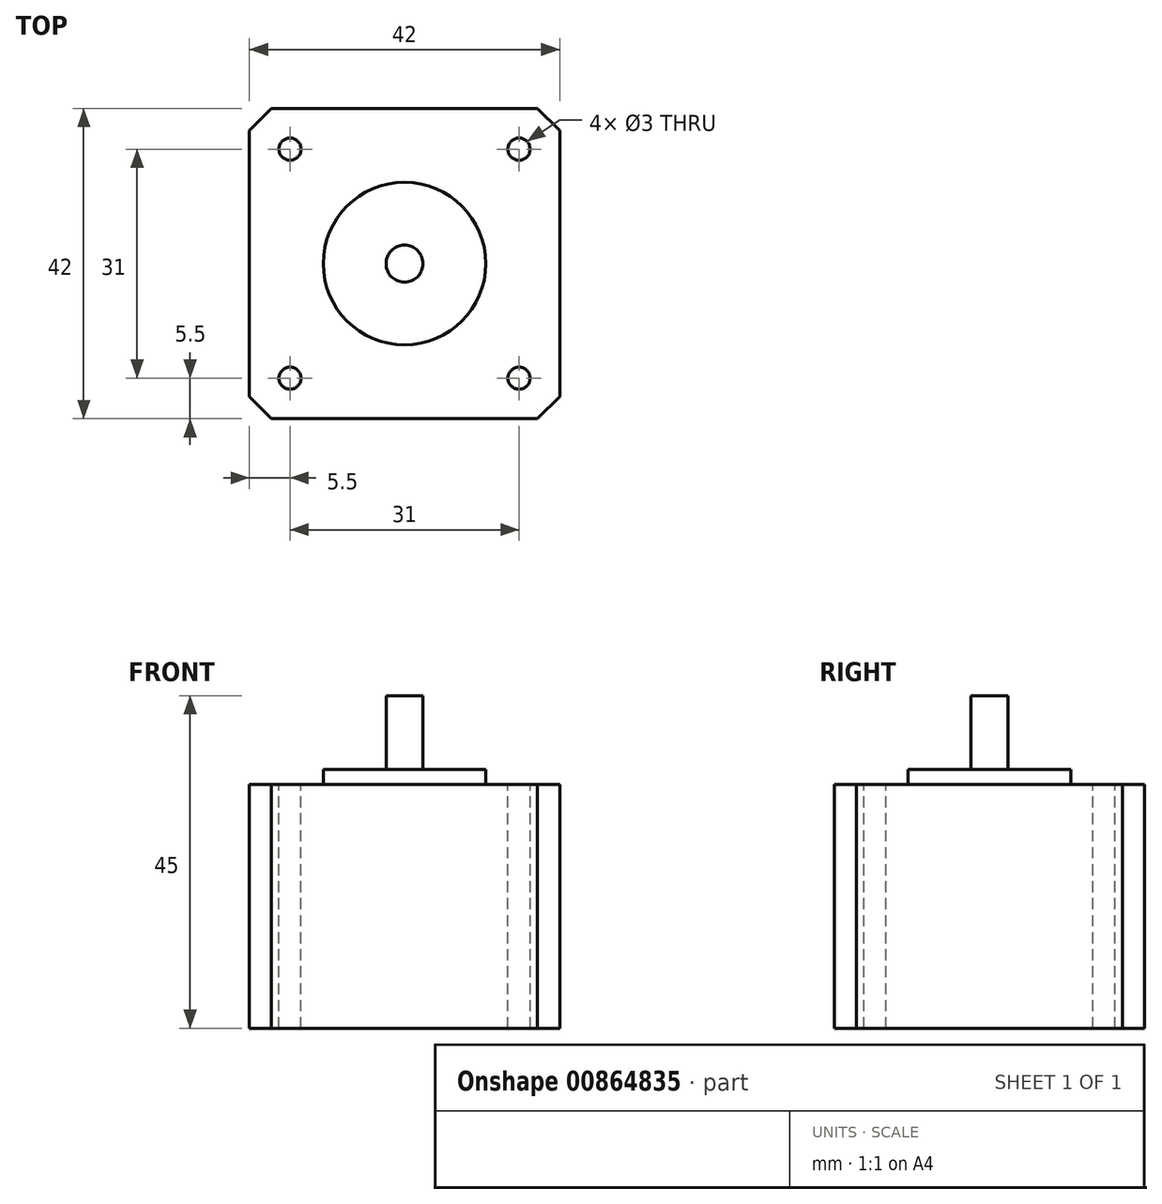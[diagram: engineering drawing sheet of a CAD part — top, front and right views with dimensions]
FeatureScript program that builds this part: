
annotation { "Feature Type Name" : "Feature", "Feature Type Description" : "" }
export const myFeature = defineFeature(function(context is Context, id is Id, definition is map)
    precondition{}
    {
        {
            var Q0;
            Q0=qCreatedBy(makeId("Top.planeOp"),FACE);
            var sketch = newSketch(context, id + "F0", { "sketchPlane" : qUnion([Q0])});
            skLineSegment(sketch, "E0.bottom", {"start": v(21, -21) * mm, "end": v(-21, -21) * mm});
            skLineSegment(sketch, "E0.top", {"start": v(21, 21) * mm, "end": v(-21, 21) * mm});
            skLineSegment(sketch, "E0.left", {"start": v(21, -21) * mm, "end": v(21, 21) * mm});
            skLineSegment(sketch, "E0.right", {"start": v(-21, -21) * mm, "end": v(-21, 21) * mm});
            skPoint(sketch, "E0.middle", {"position": v(0, 0) * mm});
            skSolve(sketch);
        }
        {
            var Q0;
            Q0 = qSketchRegion(id + "F0", true);
            extrude(context, id + "F1", {"entities" : qUnion([Q0]), "depth" : 33 * mm, "offsetDistance" : 25 * mm});
        }
        {
            var Q0;
            Q0=makeQuery(id+"F1.opExtrude","CAP_FACE",FACE,{"disambiguationData":[OSD([sQuery(id+"F0.wireOp",EDGE,"E0.bottom"),sQuery(id+"F0.wireOp",EDGE,"E0.top"),sQuery(id+"F0.wireOp",EDGE,"E0.left"),sQuery(id+"F0.wireOp",EDGE,"E0.right")])],"isStart":false});
            var sketch = newSketch(context, id + "F2", { "sketchPlane" : qUnion([Q0])});
            skCircle(sketch, "E1", {"center": v(0, 0) * mm, "radius": 11 * mm});
            skSolve(sketch);
        }
        {
            var Q0;
            Q0=makeQuery(id+"F2.imprint","IMPRINT",FACE,{"disambiguationData":[TD([[makeQuery(id+"F2.imprint","IMPRINT",EDGE,{"derivedFrom":sQuery(id+"F2.wireOp",EDGE,"E1")}),1.0]])]});
            extrude(context, id + "F3", {"entities" : qUnion([Q0]), "operationType" : NewBodyOperationType.ADD, "depth" : 2 * mm, "offsetDistance" : 25 * mm});
        }
        {
            var Q0;
            Q0=makeQuery(id+"F3.opExtrude","CAP_FACE",FACE,{"disambiguationData":[OSD([sQuery(id+"F2.wireOp",EDGE,"E1")])],"isStart":false});
            var sketch = newSketch(context, id + "F4", { "sketchPlane" : qUnion([Q0])});
            skCircle(sketch, "E2", {"center": v(0, 0) * mm, "radius": 2.5 * mm});
            skSolve(sketch);
        }
        {
            var Q0;
            Q0=makeQuery(id+"F4.imprint","IMPRINT",FACE,{"disambiguationData":[TD([[makeQuery(id+"F4.imprint","IMPRINT",EDGE,{"derivedFrom":sQuery(id+"F4.wireOp",EDGE,"E2")}),1.0]])]});
            extrude(context, id + "F5", {"entities" : qUnion([Q0]), "operationType" : NewBodyOperationType.ADD, "depth" : 10 * mm, "offsetDistance" : 25 * mm});
        }
        {
            var Q0;
            Q0=makeQuery(id+"F1.opExtrude","CAP_FACE",FACE,{"disambiguationData":[OSD([sQuery(id+"F0.wireOp",EDGE,"E0.bottom"),sQuery(id+"F0.wireOp",EDGE,"E0.top"),sQuery(id+"F0.wireOp",EDGE,"E0.left"),sQuery(id+"F0.wireOp",EDGE,"E0.right")])],"isStart":false});
            var sketch = newSketch(context, id + "F6", { "sketchPlane" : qUnion([Q0])});
            skCircle(sketch, "E3", {"center": v(-15.5, 15.5) * mm, "radius": 1.5 * mm});
            skCircle(sketch, "E4", {"center": v(15.5, 15.5) * mm, "radius": 1.5 * mm});
            skCircle(sketch, "E5", {"center": v(15.5, -15.5) * mm, "radius": 1.5 * mm});
            skCircle(sketch, "E6", {"center": v(-15.5, -15.5) * mm, "radius": 1.5 * mm});
            skSolve(sketch);
        }
        {
            var Q0;
            Q0 = qSketchRegion(id + "F6", true);
            extrude(context, id + "F7", {"entities" : qUnion([Q0]), "operationType" : NewBodyOperationType.REMOVE, "endBound" : BoundingType.THROUGH_ALL, "oppositeDirection" : true, "depth" : 25 * mm, "offsetDistance" : 25 * mm});
        }
        {
            var Q0;
            Q0=makeQuery(id+"F1.opExtrude","SWEPT_EDGE",EDGE,{"disambiguationData":[OSD([sQuery(id+"F0.wireOp",EDGE,"E0.top"),sQuery(id+"F0.wireOp",EDGE,"E0.right")])]});
            var Q1;
            Q1=makeQuery(id+"F1.opExtrude","SWEPT_EDGE",EDGE,{"disambiguationData":[OSD([sQuery(id+"F0.wireOp",EDGE,"E0.top"),sQuery(id+"F0.wireOp",EDGE,"E0.left")])]});
            var Q2;
            Q2=makeQuery(id+"F1.opExtrude","SWEPT_EDGE",EDGE,{"disambiguationData":[OSD([sQuery(id+"F0.wireOp",EDGE,"E0.bottom"),sQuery(id+"F0.wireOp",EDGE,"E0.left")])]});
            var Q3;
            Q3=makeQuery(id+"F1.opExtrude","SWEPT_EDGE",EDGE,{"disambiguationData":[OSD([sQuery(id+"F0.wireOp",EDGE,"E0.bottom"),sQuery(id+"F0.wireOp",EDGE,"E0.right")])]});
            chamfer(context, id + "F8", {"entities" : qUnion([Q0, Q1, Q2, Q3]), "width" : 3 * mm, "tangentPropagation" : true});
        }
    });
